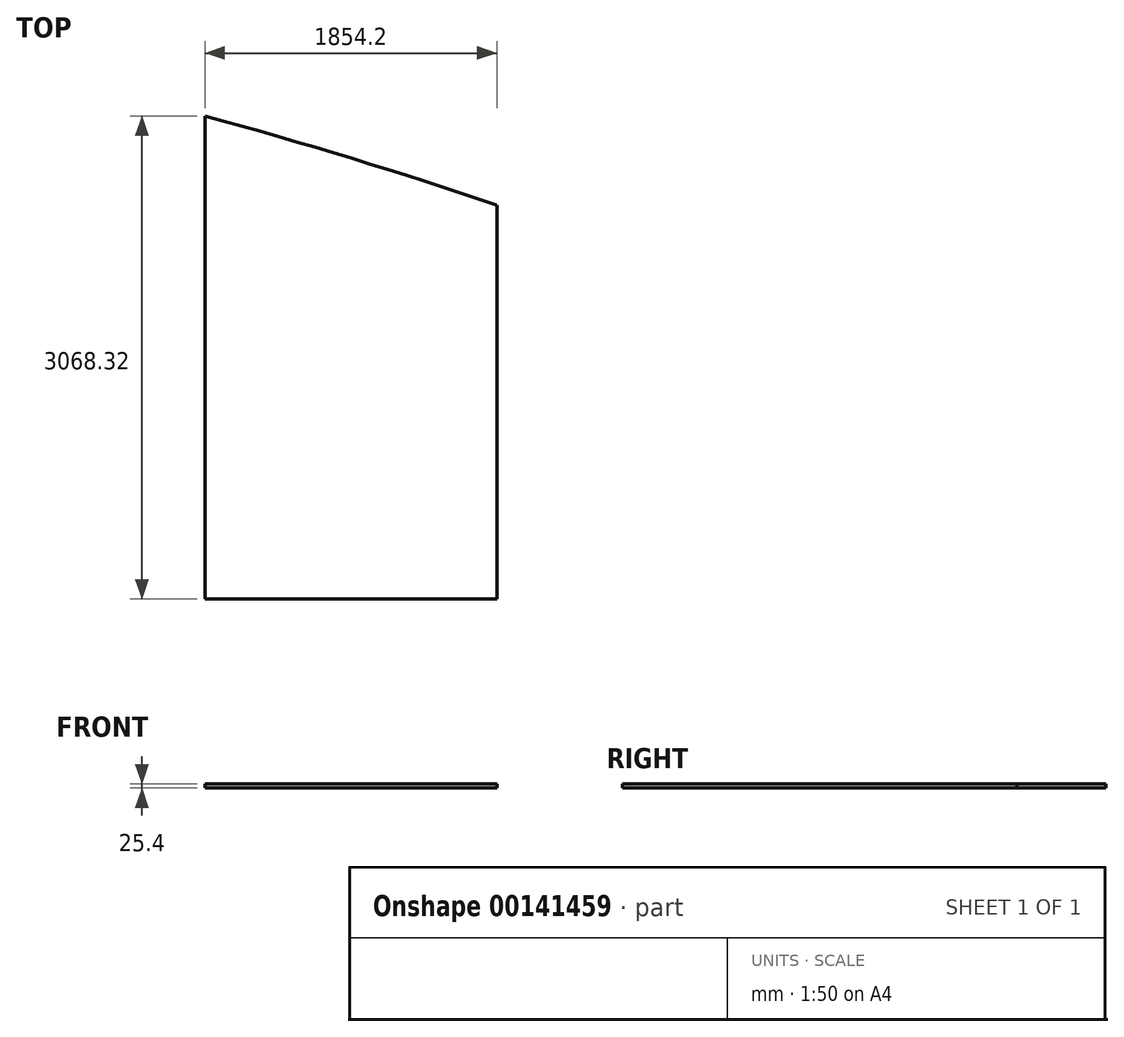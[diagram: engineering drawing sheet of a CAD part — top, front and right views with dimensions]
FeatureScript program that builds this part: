
annotation { "Feature Type Name" : "Feature", "Feature Type Description" : "" }
export const myFeature = defineFeature(function(context is Context, id is Id, definition is map)
    precondition{}
    {
        {
            var Q0;
            Q0=qCreatedBy(makeId("Top.planeOp"),FACE);
            var sketch = newSketch(context, id + "F0", { "sketchPlane" : qUnion([Q0])});
            skLineSegment(sketch, "E0", {"start": v(-927.2, -959.41) * mm, "end": v(927, -959.41) * mm});
            skLineSegment(sketch, "E1", {"start": v(-927.2, -959.41) * mm, "end": v(-927.2, 2108.9) * mm});
            skLineSegment(sketch, "E2", {"start": v(927, -959.41) * mm, "end": v(927, 1543) * mm});
            skLineSegment(sketch, "E3", {"start": v(-0.1, -959.41) * mm, "end": v(-0.1, 1841.45) * mm});
            skArc(sketch, "E4", {"start": v(927, 1543) * mm, "mid": v(4.22, 1840.13) * mm, "end": v(-927.2, 2108.9) * mm});
            skSolve(sketch);
        }
        {
            var Q0;
            {var subQ0=sQuery(id+"F0.wireOp",EDGE,"E1");Q0=makeQuery(id+"F0.imprint","IMPRINT",FACE,{"disambiguationData":[TD([[makeQuery(id+"F0.imprint","IMPRINT",EDGE,{"derivedFrom":subQ0}),-1.0]])]});}
            var Q1;
            {var subQ0=sQuery(id+"F0.wireOp",EDGE,"E2");Q1=makeQuery(id+"F0.imprint","IMPRINT",FACE,{"disambiguationData":[TD([[makeQuery(id+"F0.imprint","IMPRINT",EDGE,{"derivedFrom":subQ0}),1.0]])]});}
            extrude(context, id + "F1", {"entities" : qUnion([Q0, Q1]), "depth" : 25.4 * mm});
        }
    });
